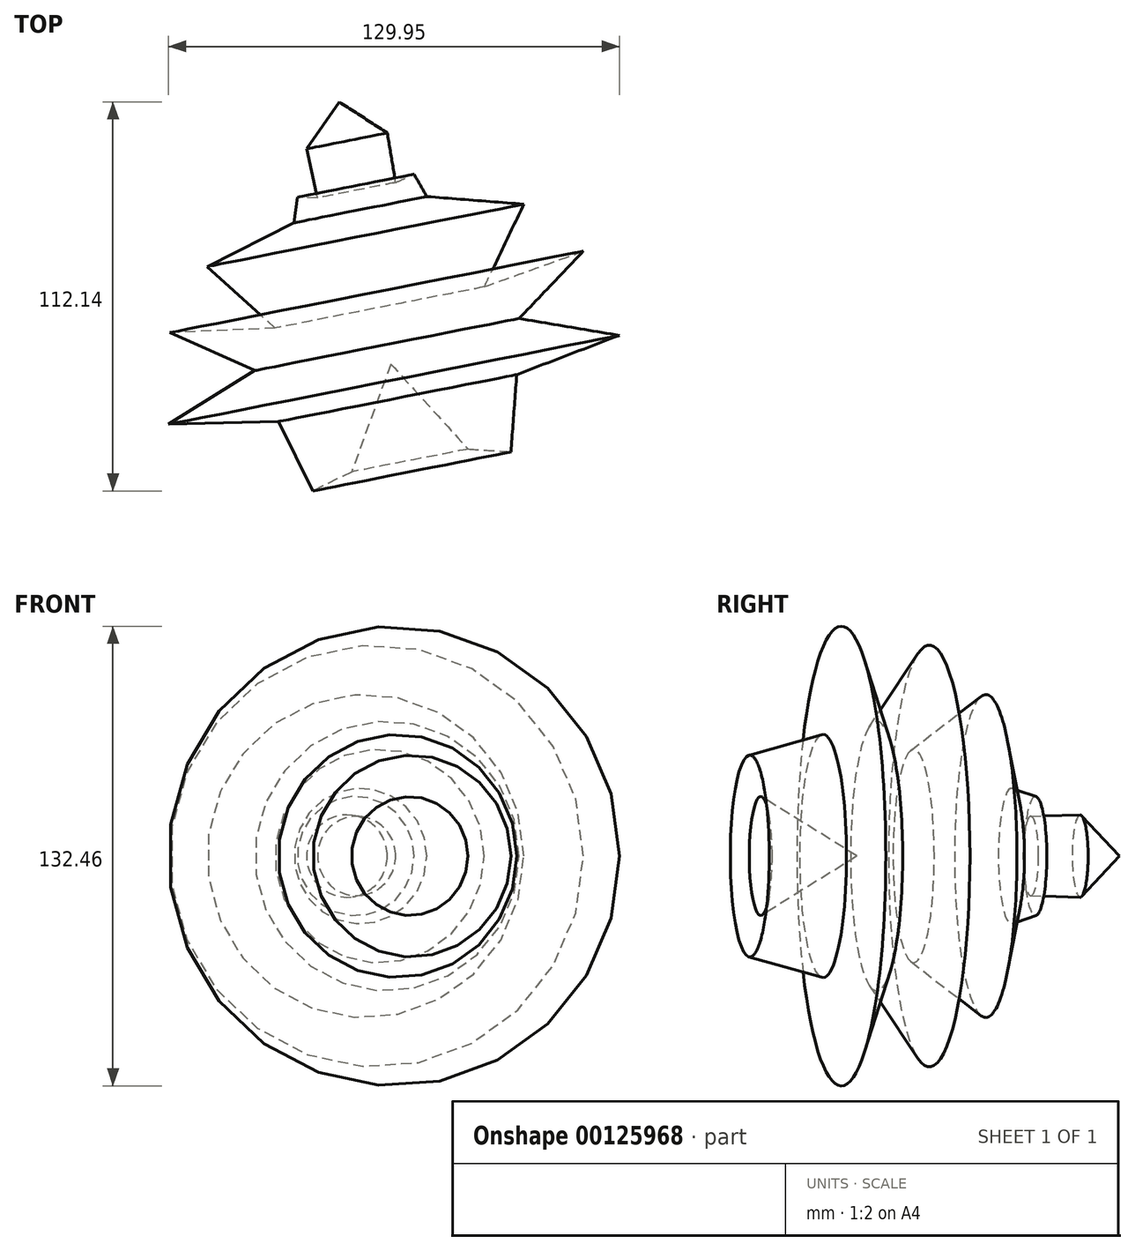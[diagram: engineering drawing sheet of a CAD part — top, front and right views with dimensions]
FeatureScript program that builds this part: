
annotation { "Feature Type Name" : "Feature", "Feature Type Description" : "" }
export const myFeature = defineFeature(function(context is Context, id is Id, definition is map)
    precondition{}
    {
        {
            var Q0;
            Q0=qCreatedBy(makeId("Top.planeOp"),FACE);
            var sketch = newSketch(context, id + "F0", { "sketchPlane" : qUnion([Q0])});
            skLineSegment(sketch, "E0", {"start": v(-24.31, 26.3) * mm, "end": v(-49.38, 13.66) * mm});
            skLineSegment(sketch, "E1", {"start": v(-49.38, 13.66) * mm, "end": v(-29.78, -4.05) * mm});
            skLineSegment(sketch, "E2", {"start": v(-29.78, -4.05) * mm, "end": v(-60.13, -5.37) * mm});
            skLineSegment(sketch, "E3", {"start": v(-60.13, -5.37) * mm, "end": v(-35.62, -16.3) * mm});
            skLineSegment(sketch, "E4", {"start": v(-35.62, -16.3) * mm, "end": v(-60.5, -31.76) * mm});
            skLineSegment(sketch, "E5", {"start": v(-60.5, -31.76) * mm, "end": v(-28.84, -31) * mm});
            skLineSegment(sketch, "E6", {"start": v(-28.84, -31) * mm, "end": v(-18.85, -50.98) * mm});
            skLineSegment(sketch, "E7", {"start": v(-18.85, -50.98) * mm, "end": v(-7.73, -45.52) * mm});
            skLineSegment(sketch, "E8", {"start": v(-7.73, -45.52) * mm, "end": v(3.58, -14.42) * mm});
            skLineSegment(sketch, "E9", {"start": v(3.58, -14.42) * mm, "end": v(-11.3, 61.16) * mm});
            skLineSegment(sketch, "E10", {"start": v(-11.3, 61.16) * mm, "end": v(-20.73, 47.6) * mm});
            skLineSegment(sketch, "E11", {"start": v(-20.73, 47.6) * mm, "end": v(-17.53, 33.46) * mm});
            skLineSegment(sketch, "E12", {"start": v(-17.53, 33.46) * mm, "end": v(-23.37, 33.64) * mm});
            skLineSegment(sketch, "E13", {"start": v(-23.37, 33.64) * mm, "end": v(-24.31, 26.3) * mm});
            skSolve(sketch);
        }
        {
            var Q0;
            Q0 = qSketchRegion(id + "F0", true);
            var Q1;
            Q1=sQuery(id+"F0.wireOp",EDGE,"E9");
            revolve(context, id + "F1", {"entities" : qUnion([Q0]), "axis" : qUnion([Q1]), "revolveType" : RevolveType.FULL});
        }
    });
